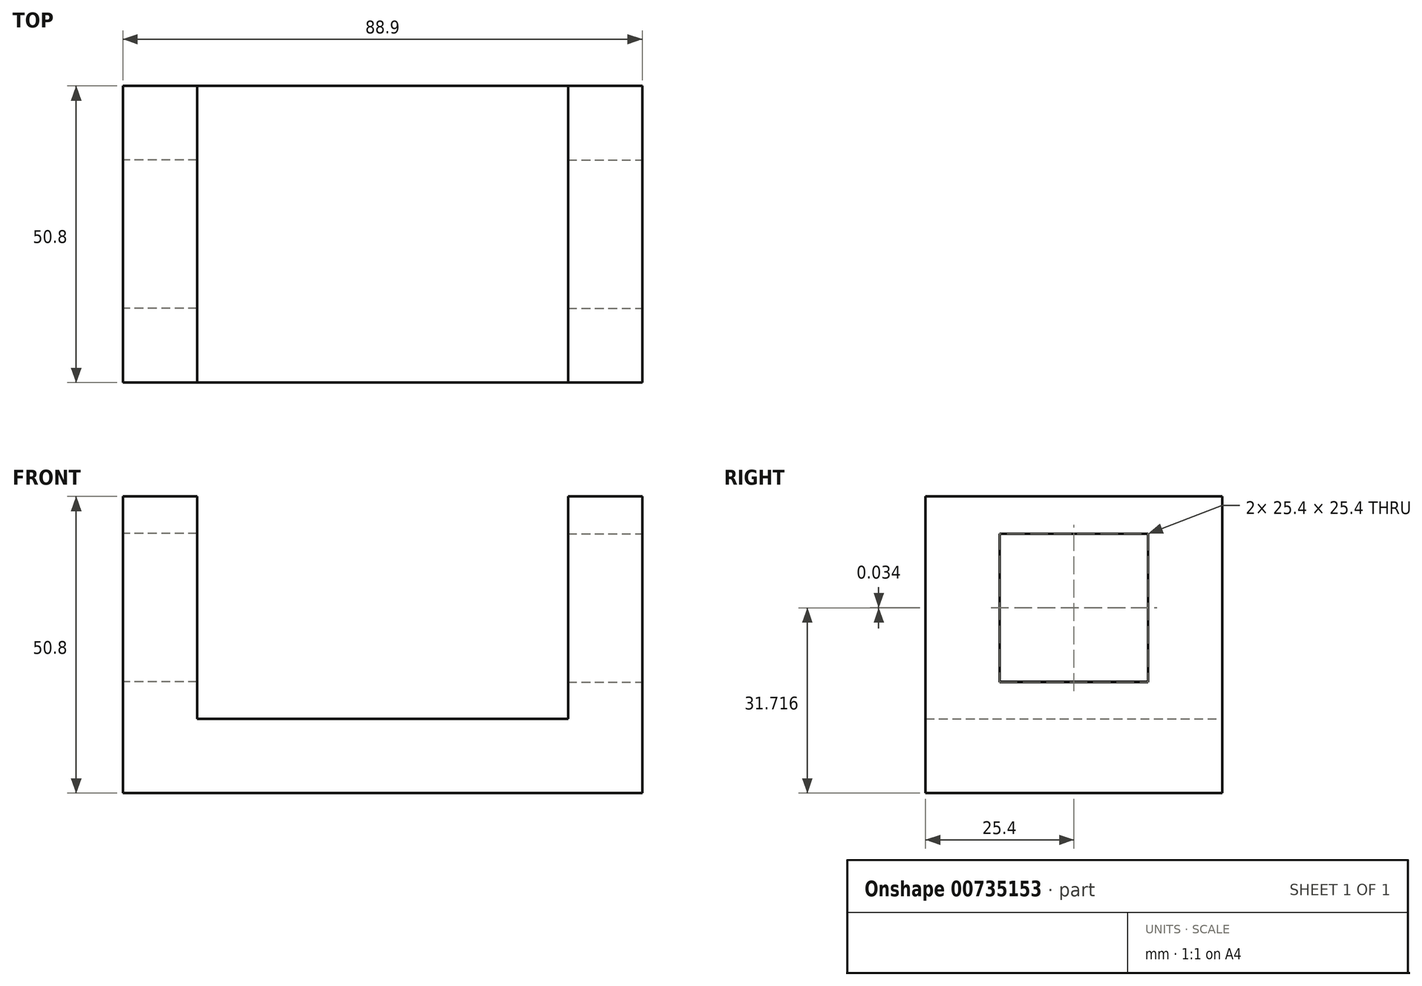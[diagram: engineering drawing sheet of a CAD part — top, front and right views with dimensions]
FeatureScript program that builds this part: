
annotation { "Feature Type Name" : "Feature", "Feature Type Description" : "" }
export const myFeature = defineFeature(function(context is Context, id is Id, definition is map)
    precondition{}
    {
        {
            var Q0;
            Q0=qCreatedBy(makeId("Front.planeOp"),FACE);
            var sketch = newSketch(context, id + "F0", { "sketchPlane" : qUnion([Q0])});
            skLineSegment(sketch, "E0", {"start": v(21.67, 31.27) * mm, "end": v(34.37, 31.27) * mm});
            skLineSegment(sketch, "E1", {"start": v(34.37, 31.27) * mm, "end": v(34.37, -19.53) * mm});
            skLineSegment(sketch, "E2", {"start": v(34.37, -19.53) * mm, "end": v(-54.53, -19.53) * mm});
            skLineSegment(sketch, "E3", {"start": v(-54.53, -19.53) * mm, "end": v(-54.53, 31.27) * mm});
            skLineSegment(sketch, "E4", {"start": v(-54.53, 31.27) * mm, "end": v(-41.83, 31.27) * mm});
            skLineSegment(sketch, "E5", {"start": v(-41.83, 31.27) * mm, "end": v(-41.83, -6.83) * mm});
            skLineSegment(sketch, "E6", {"start": v(-41.83, -6.83) * mm, "end": v(21.67, -6.83) * mm});
            skLineSegment(sketch, "E7", {"start": v(21.67, -6.83) * mm, "end": v(21.67, 31.27) * mm});
            skSolve(sketch);
        }
        {
            var Q0;
            Q0=makeQuery(id+"F0.imprint","IMPRINT",FACE,{"disambiguationData":[TD([[makeQuery(id+"F0.imprint","IMPRINT",EDGE,{"derivedFrom":sQuery(id+"F0.wireOp",EDGE,"E0")}),-1.0]])]});
            extrude(context, id + "F1", {"entities" : qUnion([Q0]), "depth" : 50.8 * mm, "offsetDistance" : 25.4 * mm});
        }
        {
            var Q0;
            Q0=makeQuery(id+"F1.opExtrude","SWEPT_FACE",FACE,{"disambiguationData":[OSD([sQuery(id+"F0.wireOp",EDGE,"E1")])]});
            var sketch = newSketch(context, id + "F2", { "sketchPlane" : qUnion([Q0])});
            skLineSegment(sketch, "E8.bottom", {"start": v(-38.1, 24.89) * mm, "end": v(-12.7, 24.89) * mm});
            skLineSegment(sketch, "E8.top", {"start": v(-38.1, -0.51) * mm, "end": v(-12.7, -0.51) * mm});
            skLineSegment(sketch, "E8.left", {"start": v(-38.1, 24.89) * mm, "end": v(-38.1, -0.51) * mm});
            skLineSegment(sketch, "E8.right", {"start": v(-12.7, 24.89) * mm, "end": v(-12.7, -0.51) * mm});
            skLineSegment(sketch, "E9", {"start": v(-23.61, -0.51) * mm, "end": v(-24.74, -19.53) * mm});
            skLineSegment(sketch, "E10", {"start": v(-38.1, 13.35) * mm, "end": v(-50.8, 13.35) * mm});
            skSolve(sketch);
        }
        {
            var Q0;
            {var subQ1=sQuery(id+"F2.wireOp",EDGE,"E8.bottom");Q0=makeQuery(id+"F2.imprint","IMPRINT",FACE,{"disambiguationData":[TD([[makeQuery(id+"F2.imprint","IMPRINT",EDGE,{"derivedFrom":subQ1}),-1.0]])]});}
            extrude(context, id + "F3", {"entities" : qUnion([Q0]), "operationType" : NewBodyOperationType.REMOVE, "oppositeDirection" : true, "depth" : 12.7 * mm, "offsetDistance" : 25.4 * mm});
        }
        {
            var Q0;
            Q0=makeQuery(id+"F1.opExtrude","SWEPT_FACE",FACE,{"disambiguationData":[OSD([sQuery(id+"F0.wireOp",EDGE,"E3")])]});
            var sketch = newSketch(context, id + "F4", { "sketchPlane" : qUnion([Q0])});
            skLineSegment(sketch, "E11.bottom", {"start": v(12.7, 24.92) * mm, "end": v(38.1, 24.92) * mm});
            skLineSegment(sketch, "E11.top", {"start": v(12.7, -0.48) * mm, "end": v(38.1, -0.48) * mm});
            skLineSegment(sketch, "E11.left", {"start": v(12.7, 24.92) * mm, "end": v(12.7, -0.48) * mm});
            skLineSegment(sketch, "E11.right", {"start": v(38.1, 24.92) * mm, "end": v(38.1, -0.48) * mm});
            skLineSegment(sketch, "E12", {"start": v(12.7, 9) * mm, "end": v(0, 9) * mm});
            skLineSegment(sketch, "E13", {"start": v(25.4, -0.48) * mm, "end": v(25.4, -19.53) * mm});
            skSolve(sketch);
        }
        {
            var Q0;
            {var subQ1=sQuery(id+"F4.wireOp",EDGE,"E11.bottom");Q0=makeQuery(id+"F4.imprint","IMPRINT",FACE,{"disambiguationData":[TD([[makeQuery(id+"F4.imprint","IMPRINT",EDGE,{"derivedFrom":subQ1}),-1.0]])]});}
            extrude(context, id + "F5", {"entities" : qUnion([Q0]), "operationType" : NewBodyOperationType.REMOVE, "oppositeDirection" : true, "depth" : 12.7 * mm, "offsetDistance" : 25.4 * mm});
        }
    });
